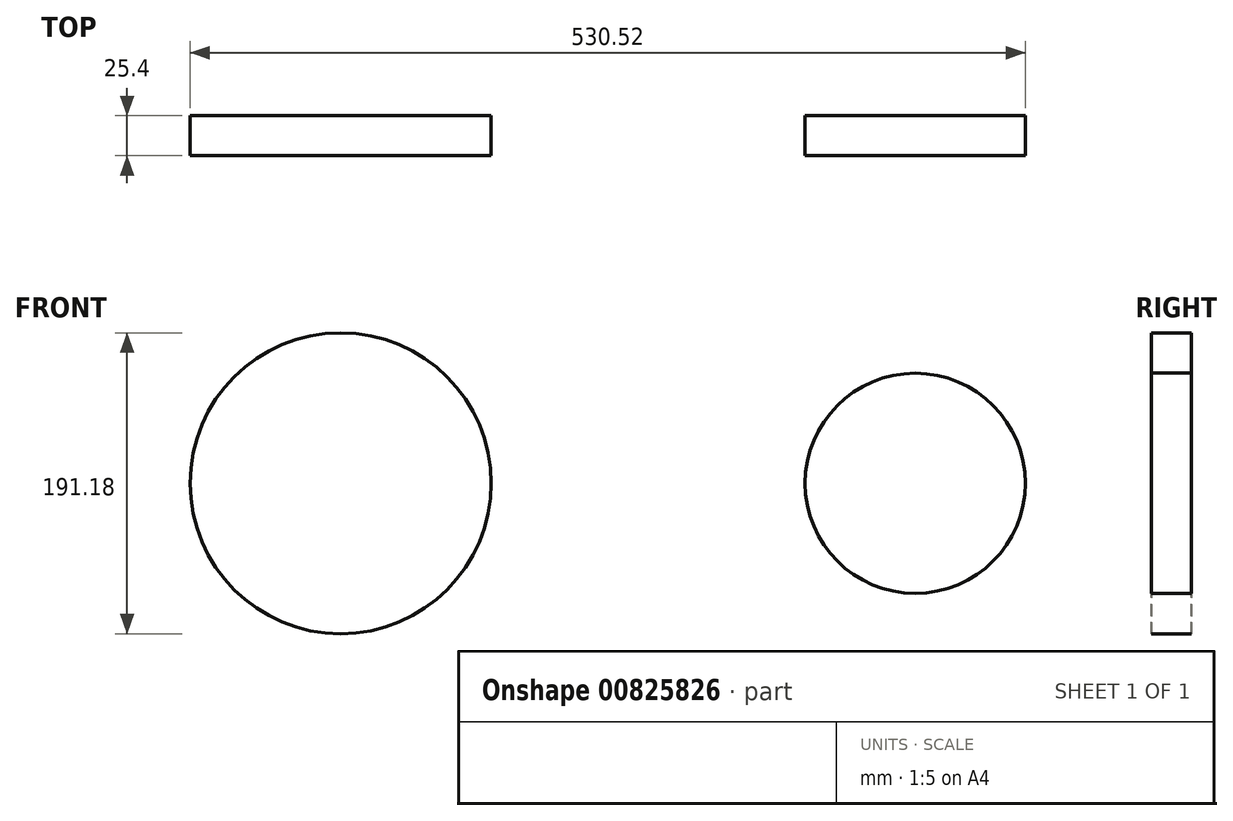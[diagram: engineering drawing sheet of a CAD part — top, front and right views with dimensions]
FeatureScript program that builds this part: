
annotation { "Feature Type Name" : "Feature", "Feature Type Description" : "" }
export const myFeature = defineFeature(function(context is Context, id is Id, definition is map)
    precondition{}
    {
        {
            var Q0;
            Q0=qCreatedBy(makeId("Front.planeOp"),FACE);
            var sketch = newSketch(context, id + "F0", { "sketchPlane" : qUnion([Q0])});
            skCircle(sketch, "E0", {"center": v(0, 0) * mm, "radius": 95.59 * mm});
            skSolve(sketch);
        }
        {
            var Q0;
            Q0=qCreatedBy(makeId("Front.planeOp"),FACE);
            var sketch = newSketch(context, id + "F1", { "sketchPlane" : qUnion([Q0])});
            skCircle(sketch, "E1", {"center": v(364.98, 0) * mm, "radius": 69.94 * mm});
            skSolve(sketch);
        }
        {
            var Q0;
            Q0=makeQuery(id+"F0.imprint","IMPRINT",FACE,{"disambiguationData":[TD([[makeQuery(id+"F0.imprint","IMPRINT",EDGE,{"derivedFrom":sQuery(id+"F0.wireOp",EDGE,"E0")}),1.0]])]});
            var sketch = newSketch(context, id + "F2", { "sketchPlane" : qUnion([Q0])});
            skLineSegment(sketch, "E2", {"start": v(77.02, -56.8) * mm, "end": v(323.66, -56.8) * mm});
            skSolve(sketch);
        }
        {
            var Q0;
            Q0=makeQuery(id+"F1.imprint","IMPRINT",FACE,{"disambiguationData":[TD([[makeQuery(id+"F1.imprint","IMPRINT",EDGE,{"derivedFrom":sQuery(id+"F1.wireOp",EDGE,"E1")}),1.0]])]});
            var Q1;
            Q1=makeQuery(id+"F0.imprint","IMPRINT",FACE,{"disambiguationData":[TD([[makeQuery(id+"F0.imprint","IMPRINT",EDGE,{"derivedFrom":sQuery(id+"F0.wireOp",EDGE,"E0")}),1.0]])]});
            extrude(context, id + "F3", {"entities" : qUnion([Q0, Q1]), "oppositeDirection" : true, "depth" : 25.4 * mm, "offsetDistance" : 25.4 * mm});
        }
    });
